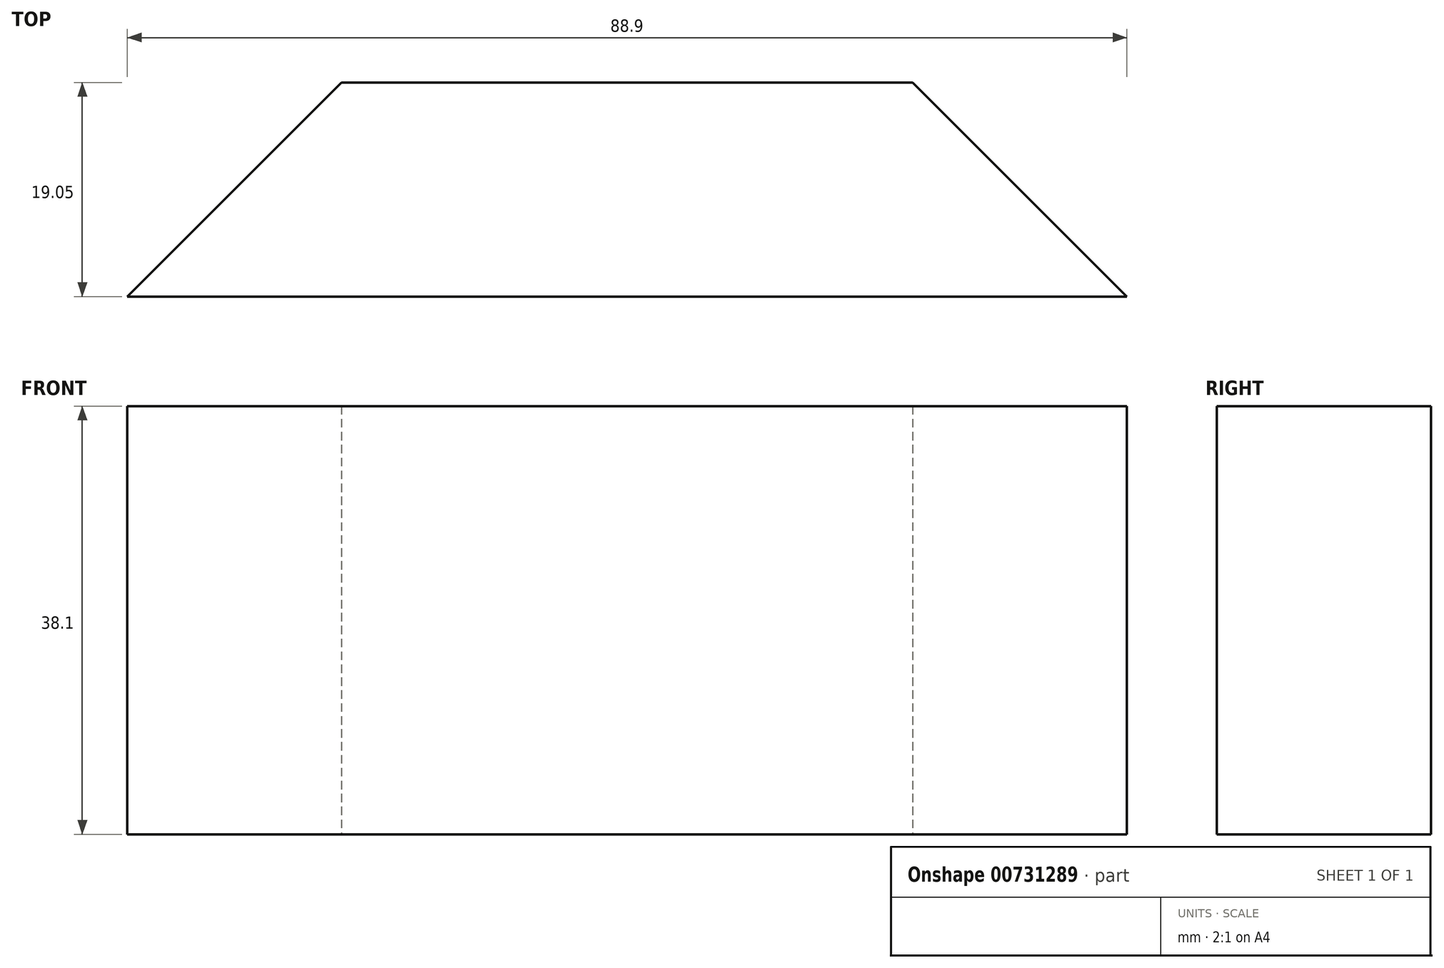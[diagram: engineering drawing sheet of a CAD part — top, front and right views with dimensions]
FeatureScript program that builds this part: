
annotation { "Feature Type Name" : "Feature", "Feature Type Description" : "" }
export const myFeature = defineFeature(function(context is Context, id is Id, definition is map)
    precondition{}
    {
        {
            var Q0;
            Q0=qCreatedBy(makeId("Top.planeOp"),FACE);
            var sketch = newSketch(context, id + "F0", { "sketchPlane" : qUnion([Q0])});
            skLineSegment(sketch, "E0", {"start": v(-25.4, 19.05) * mm, "end": v(-44.45, 0) * mm});
            skLineSegment(sketch, "E1", {"start": v(-44.45, 0) * mm, "end": v(44.45, 0) * mm});
            skLineSegment(sketch, "E2", {"start": v(44.45, 0) * mm, "end": v(25.4, 19.05) * mm});
            skLineSegment(sketch, "E3", {"start": v(25.4, 19.05) * mm, "end": v(-25.4, 19.05) * mm});
            skSolve(sketch);
        }
        {
            var Q0;
            Q0 = qSketchRegion(id + "F0", true);
            extrude(context, id + "F1", {"entities" : qUnion([Q0]), "depth" : 25.4 * mm, "offsetDistance" : 25.4 * mm});
        }
        {
            var Q0;
            Q0=makeQuery(id+"F1.opExtrude","CAP_FACE",FACE,{"disambiguationData":[OSD([sQuery(id+"F0.wireOp",EDGE,"E0"),sQuery(id+"F0.wireOp",EDGE,"E1"),sQuery(id+"F0.wireOp",EDGE,"E2"),sQuery(id+"F0.wireOp",EDGE,"E3")])],"isStart":false});
            extrude(context, id + "F2", {"entities" : qUnion([Q0]), "operationType" : NewBodyOperationType.ADD, "depth" : 12.7 * mm, "offsetDistance" : 25.4 * mm});
        }
    });
